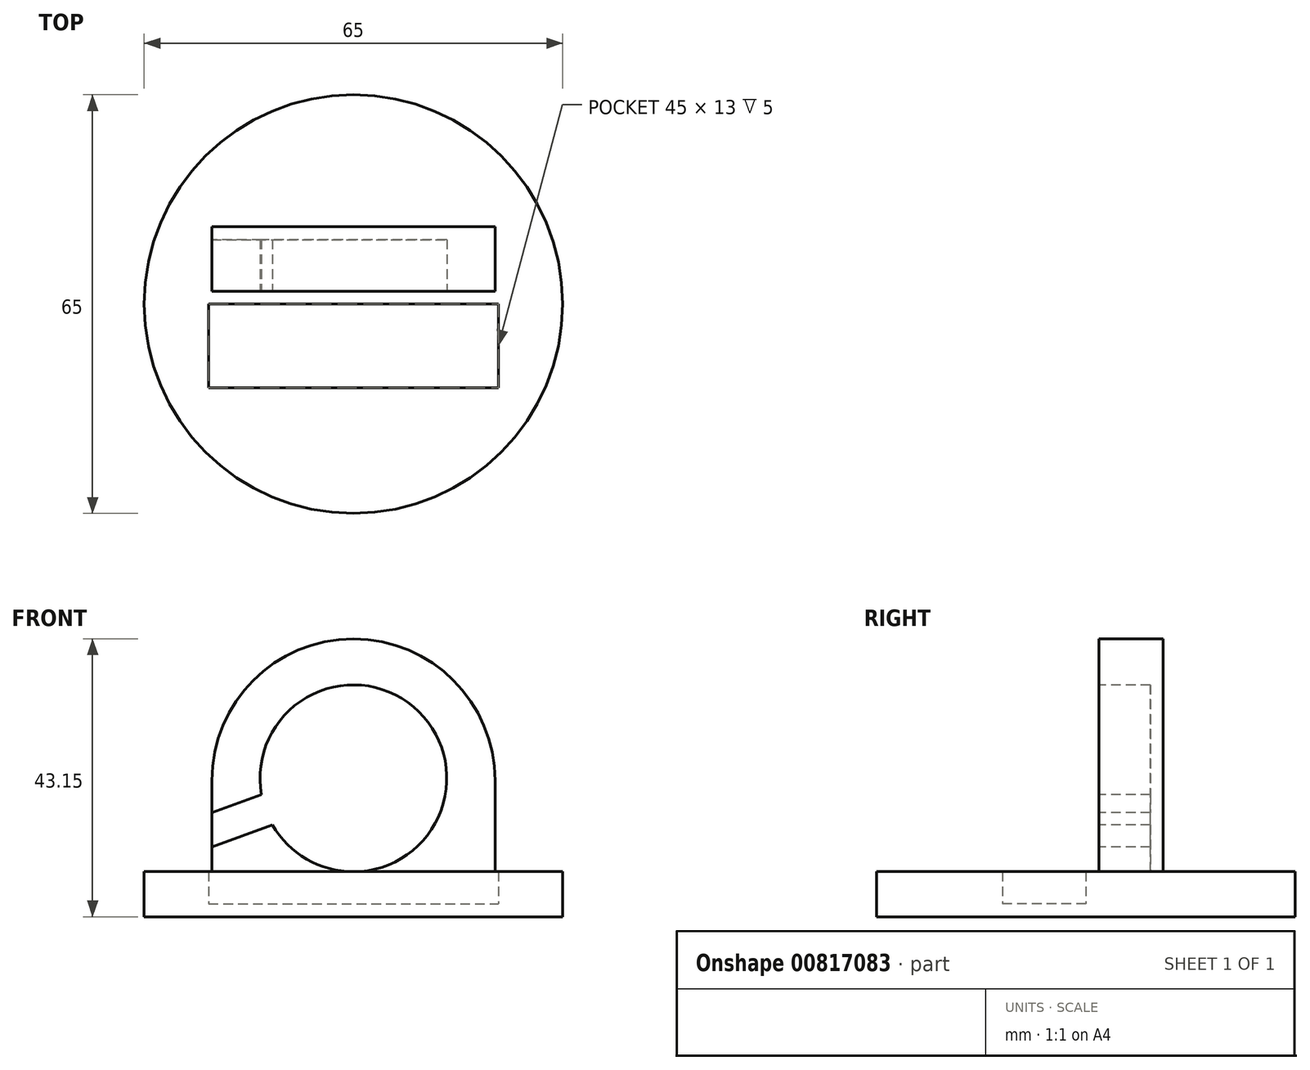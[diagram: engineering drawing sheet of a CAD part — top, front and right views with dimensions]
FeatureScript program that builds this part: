
annotation { "Feature Type Name" : "Feature", "Feature Type Description" : "" }
export const myFeature = defineFeature(function(context is Context, id is Id, definition is map)
    precondition{}
    {
        {
            var Q0;
            Q0=qCreatedBy(makeId("Top.planeOp"),FACE);
            var sketch = newSketch(context, id + "F0", { "sketchPlane" : qUnion([Q0])});
            skCircle(sketch, "E0", {"center": v(0, 0) * mm, "radius": 32.5 * mm});
            skPoint(sketch, "E1", {"position": v(-22.5, 0) * mm});
            skPoint(sketch, "E2.MirrorP", {"position": v(22.5, 0) * mm});
            skLineSegment(sketch, "E3.bottom", {"start": v(-22.5, 0) * mm, "end": v(22.5, 0) * mm});
            skLineSegment(sketch, "E3.top", {"start": v(-22.5, -13) * mm, "end": v(22.5, -13) * mm});
            skLineSegment(sketch, "E3.left", {"start": v(-22.5, 0) * mm, "end": v(-22.5, -13) * mm});
            skLineSegment(sketch, "E3.right", {"start": v(22.5, 0) * mm, "end": v(22.5, -13) * mm});
            skLineSegment(sketch, "E4", {"start": v(-32.44, 2) * mm, "end": v(32.44, 2) * mm, "construction": true});
            skSolve(sketch);
        }
        {
            var Q0;
            Q0=makeQuery(id+"F0.imprint","IMPRINT",FACE,{"disambiguationData":[TD([[makeQuery(id+"F0.imprint","IMPRINT",EDGE,{"derivedFrom":sQuery(id+"F0.wireOp",EDGE,"E0")}),1.0]])]});
            extrude(context, id + "F1", {"entities" : qUnion([Q0]), "depth" : 7 * mm, "offsetDistance" : 25 * mm});
        }
        {
            var Q0;
            Q0=makeQuery(id+"F0.imprint","IMPRINT",FACE,{"disambiguationData":[TD([[makeQuery(id+"F0.imprint","IMPRINT",EDGE,{"derivedFrom":sQuery(id+"F0.wireOp",EDGE,"E3.bottom")}),-1.0]])]});
            extrude(context, id + "F2", {"entities" : qUnion([Q0]), "operationType" : NewBodyOperationType.ADD, "depth" : 2 * mm, "offsetDistance" : 25 * mm});
        }
        {
            var Q0;
            Q0=qCreatedBy(makeId("Front.planeOp"),FACE);
            cPlane(context, id + "F3", {"entities" : qUnion([Q0]), "cplaneType" : CPlaneType.OFFSET, "offset" : 2 * mm, "oppositeDirection" : true, "width" : 150 * mm, "height" : 150 * mm});
        }
        {
            var Q0;
            Q0=qCreatedBy(id+"F3.planeOp",FACE);
            var sketch = newSketch(context, id + "F4", { "sketchPlane" : qUnion([Q0])});
            skLineSegment(sketch, "E5", {"start": v(-37.5, 7) * mm, "end": v(44.54, 7) * mm, "construction": true});
            skPoint(sketch, "E6", {"position": v(-22, 7) * mm});
            skPoint(sketch, "E7.MirrorP", {"position": v(22, 7) * mm});
            skPoint(sketch, "E8", {"position": v(-14.5, 7) * mm});
            skPoint(sketch, "E9.MirrorP", {"position": v(14.5, 7) * mm});
            skLineSegment(sketch, "E10", {"start": v(-14.5, 7) * mm, "end": v(-14.5, 35.3) * mm, "construction": true});
            skLineSegment(sketch, "E11.MirrorCS", {"start": v(14.5, 7) * mm, "end": v(14.5, 35.3) * mm, "construction": true});
            skArc(sketch, "E12", {"start": v(-12.57, 14.27) * mm, "mid": v(13.63, 26.47) * mm, "end": v(-14.28, 18.97) * mm});
            skPoint(sketch, "E12.first.point", {"position": v(0, 7) * mm});
            skPoint(sketch, "E12.second.point", {"position": v(14.5, 21.15) * mm});
            skPoint(sketch, "E12.third.point", {"position": v(-14.5, 21.15) * mm});
            skLineSegment(sketch, "E13", {"start": v(-14.5, 21.15) * mm, "end": v(-26.24, 21.15) * mm, "construction": true});
            skLineSegment(sketch, "E14.MirrorCS", {"start": v(14.5, 21.15) * mm, "end": v(26.24, 21.15) * mm, "construction": true});
            skLineSegment(sketch, "E15", {"start": v(-22, 7) * mm, "end": v(-22, 21.15) * mm});
            skLineSegment(sketch, "E16", {"start": v(-22, 7) * mm, "end": v(22, 7) * mm});
            skLineSegment(sketch, "E17", {"start": v(22, 21.15) * mm, "end": v(22, 7) * mm});
            skArc(sketch, "E18", {"start": v(22, 21.15) * mm, "mid": v(0, 43.15) * mm, "end": v(-22, 21.15) * mm});
            skLineSegment(sketch, "E19", {"start": v(-13.63, 16.54) * mm, "end": v(-37.4, 7.9) * mm, "construction": true});
            skLineSegment(sketch, "E20", {"start": v(-14.28, 18.97) * mm, "end": v(-22, 16.16) * mm});
            skLineSegment(sketch, "E21", {"start": v(-22, 10.84) * mm, "end": v(-12.57, 14.27) * mm});
            skLineSegment(sketch, "E22", {"start": v(-22, 16.16) * mm, "end": v(-22, 10.84) * mm});
            skLineSegment(sketch, "E23", {"start": v(-22, 10.84) * mm, "end": v(-32.54, 7) * mm, "construction": true});
            skSolve(sketch);
        }
        {
            var Q0;
            {var subQ0=sQuery(id+"F4.wireOp",EDGE,"E17");Q0=makeQuery(id+"F4.imprint","IMPRINT",FACE,{"disambiguationData":[TD([[makeQuery(id+"F4.imprint","IMPRINT",EDGE,{"derivedFrom":subQ0}),-1.0]])]});}
            var Q1;
            {var subQ0=sQuery(id+"F4.wireOp",EDGE,"E21");Q1=makeQuery(id+"F4.imprint","IMPRINT",FACE,{"disambiguationData":[TD([[makeQuery(id+"F4.imprint","IMPRINT",EDGE,{"derivedFrom":subQ0}),-1.0]])]});}
            extrude(context, id + "F5", {"entities" : qUnion([Q0, Q1]), "operationType" : NewBodyOperationType.ADD, "oppositeDirection" : true, "depth" : 10 * mm, "offsetDistance" : 25 * mm});
        }
        {
            var Q0;
            {var subQ1=sQuery(id+"F4.wireOp",EDGE,"E20");Q0=makeQuery(id+"F4.imprint","IMPRINT",FACE,{"disambiguationData":[TD([[makeQuery(id+"F4.imprint","IMPRINT",EDGE,{"derivedFrom":subQ1}),1.0]])]});}
            extrude(context, id + "F6", {"entities" : qUnion([Q0]), "operationType" : NewBodyOperationType.ADD, "oppositeDirection" : true, "depth" : 10 * mm, "offsetDistance" : 25 * mm, "hasSecondDirection" : true, "secondDirectionOppositeDirection" : true, "secondDirectionDepth" : 8 * mm});
        }
    });
